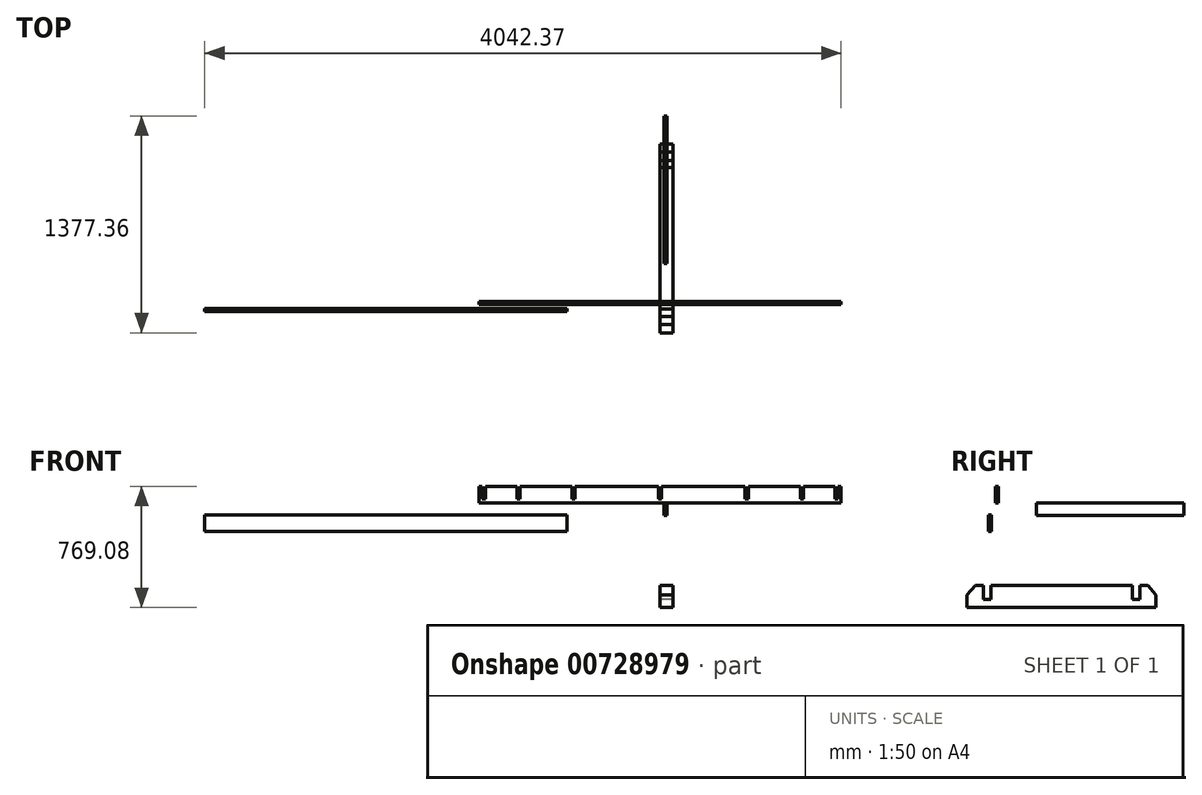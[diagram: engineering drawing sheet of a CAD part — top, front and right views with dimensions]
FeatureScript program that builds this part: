
annotation { "Feature Type Name" : "Feature", "Feature Type Description" : "" }
export const myFeature = defineFeature(function(context is Context, id is Id, definition is map)
    precondition{}
    {
        {
            var Q0;
            Q0=qCreatedBy(makeId("Front.planeOp"),FACE);
            var sketch = newSketch(context, id + "F0", { "sketchPlane" : qUnion([Q0])});
            skLineSegment(sketch, "E0.bottom", {"start": v(0, 0) * mm, "end": v(1150, 0) * mm});
            skLineSegment(sketch, "E0.top", {"start": v(10, 106) * mm, "end": v(540, 106) * mm});
            skLineSegment(sketch, "E0.right", {"start": v(1150, 0) * mm, "end": v(1150, 106) * mm});
            skLineSegment(sketch, "E1.top", {"start": v(0, 26) * mm, "end": v(10, 26) * mm});
            skLineSegment(sketch, "E1.right", {"start": v(10, 106) * mm, "end": v(10, 26) * mm});
            skLineSegment(sketch, "E2.top", {"start": v(540, 26) * mm, "end": v(560, 26) * mm});
            skLineSegment(sketch, "E2.left", {"start": v(540, 106) * mm, "end": v(540, 26) * mm});
            skLineSegment(sketch, "E2.right", {"start": v(560, 106) * mm, "end": v(560, 26) * mm});
            skLineSegment(sketch, "E3.1.0.0", {"start": v(910, 106) * mm, "end": v(910, 26) * mm});
            skLineSegment(sketch, "E3.1.0.1", {"start": v(890, 106) * mm, "end": v(890, 26) * mm});
            skLineSegment(sketch, "E3.1.0.2", {"start": v(890, 26) * mm, "end": v(910, 26) * mm});
            skLineSegment(sketch, "E3.2.0.0", {"start": v(1130, 106) * mm, "end": v(1130, 26) * mm});
            skLineSegment(sketch, "E3.2.0.1", {"start": v(1110, 106) * mm, "end": v(1110, 26) * mm});
            skLineSegment(sketch, "E3.2.0.2", {"start": v(1110, 26) * mm, "end": v(1130, 26) * mm});
            skLineSegment(sketch, "E3.direction1", {"start": v(540, 26) * mm, "end": v(890, 26) * mm, "construction": true});
            skLineSegment(sketch, "E4.trimOffspring", {"start": v(560, 106) * mm, "end": v(890, 106) * mm});
            skLineSegment(sketch, "E5.trimOffspring", {"start": v(910, 106) * mm, "end": v(1110, 106) * mm});
            skLineSegment(sketch, "E6.trimOffspring", {"start": v(1130, 106) * mm, "end": v(1150, 106) * mm});
            skLineSegment(sketch, "E7.MirrorCS", {"start": v(0, 26) * mm, "end": v(-10, 26) * mm});
            skLineSegment(sketch, "E8.MirrorCS", {"start": v(-540, 26) * mm, "end": v(-560, 26) * mm});
            skLineSegment(sketch, "E9.MirrorCS", {"start": v(-890, 26) * mm, "end": v(-910, 26) * mm});
            skLineSegment(sketch, "E10.MirrorCS", {"start": v(-1110, 26) * mm, "end": v(-1130, 26) * mm});
            skLineSegment(sketch, "E11.MirrorCS", {"start": v(-1130, 106) * mm, "end": v(-1150, 106) * mm});
            skLineSegment(sketch, "E12.MirrorCS", {"start": v(-1110, 106) * mm, "end": v(-1110, 26) * mm});
            skLineSegment(sketch, "E13.MirrorCS", {"start": v(-540, 26) * mm, "end": v(-890, 26) * mm, "construction": true});
            skLineSegment(sketch, "E14.MirrorCS", {"start": v(0, 0) * mm, "end": v(-1150, 0) * mm});
            skLineSegment(sketch, "E15.MirrorCS", {"start": v(-10, 106) * mm, "end": v(-540, 106) * mm});
            skLineSegment(sketch, "E16.MirrorCS", {"start": v(-1150, 0) * mm, "end": v(-1150, 106) * mm});
            skLineSegment(sketch, "E17.MirrorCS", {"start": v(-10, 106) * mm, "end": v(-10, 26) * mm});
            skLineSegment(sketch, "E18.MirrorCS", {"start": v(-540, 106) * mm, "end": v(-540, 26) * mm});
            skLineSegment(sketch, "E19.MirrorCS", {"start": v(-560, 106) * mm, "end": v(-560, 26) * mm});
            skLineSegment(sketch, "E20.MirrorCS", {"start": v(-910, 106) * mm, "end": v(-910, 26) * mm});
            skLineSegment(sketch, "E21.MirrorCS", {"start": v(-890, 106) * mm, "end": v(-890, 26) * mm});
            skLineSegment(sketch, "E22.MirrorCS", {"start": v(-1130, 106) * mm, "end": v(-1130, 26) * mm});
            skLineSegment(sketch, "E23.MirrorCS", {"start": v(-560, 106) * mm, "end": v(-890, 106) * mm});
            skLineSegment(sketch, "E24.MirrorCS", {"start": v(-910, 106) * mm, "end": v(-1110, 106) * mm});
            skSolve(sketch);
        }
        {
            var Q0;
            Q0=makeQuery(id+"F0.imprint","IMPRINT",FACE,{"disambiguationData":[TD([[makeQuery(id+"F0.imprint","IMPRINT",EDGE,{"derivedFrom":sQuery(id+"F0.wireOp",EDGE,"E0.bottom")}),1.0]])]});
            extrude(context, id + "F1", {"entities" : qUnion([Q0]), "depth" : 19 * mm, "offsetDistance" : 25 * mm});
        }
        {
            var Q0;
            Q0=makeQuery(id+"F1.opExtrude","CAP_FACE",FACE,{"disambiguationData":[OSD([sQuery(id+"F0.wireOp",EDGE,"E0.bottom"),sQuery(id+"F0.wireOp",EDGE,"E0.top"),sQuery(id+"F0.wireOp",EDGE,"E0.right"),sQuery(id+"F0.wireOp",EDGE,"E1.top"),sQuery(id+"F0.wireOp",EDGE,"E1.right"),sQuery(id+"F0.wireOp",EDGE,"E2.top"),sQuery(id+"F0.wireOp",EDGE,"E2.left"),sQuery(id+"F0.wireOp",EDGE,"E2.right"),sQuery(id+"F0.wireOp",EDGE,"E3.1.0.0"),sQuery(id+"F0.wireOp",EDGE,"E3.1.0.1"),sQuery(id+"F0.wireOp",EDGE,"E3.1.0.2"),sQuery(id+"F0.wireOp",EDGE,"E3.2.0.0"),sQuery(id+"F0.wireOp",EDGE,"E3.2.0.1"),sQuery(id+"F0.wireOp",EDGE,"E3.2.0.2"),sQuery(id+"F0.wireOp",EDGE,"E4.trimOffspring"),sQuery(id+"F0.wireOp",EDGE,"E5.trimOffspring"),sQuery(id+"F0.wireOp",EDGE,"E6.trimOffspring"),sQuery(id+"F0.wireOp",EDGE,"E7.MirrorCS"),sQuery(id+"F0.wireOp",EDGE,"E8.MirrorCS"),sQuery(id+"F0.wireOp",EDGE,"E9.MirrorCS"),sQuery(id+"F0.wireOp",EDGE,"E10.MirrorCS"),sQuery(id+"F0.wireOp",EDGE,"E11.MirrorCS"),sQuery(id+"F0.wireOp",EDGE,"E12.MirrorCS"),sQuery(id+"F0.wireOp",EDGE,"E14.MirrorCS"),sQuery(id+"F0.wireOp",EDGE,"E15.MirrorCS"),sQuery(id+"F0.wireOp",EDGE,"E16.MirrorCS"),sQuery(id+"F0.wireOp",EDGE,"E17.MirrorCS"),sQuery(id+"F0.wireOp",EDGE,"E18.MirrorCS"),sQuery(id+"F0.wireOp",EDGE,"E19.MirrorCS"),sQuery(id+"F0.wireOp",EDGE,"E20.MirrorCS"),sQuery(id+"F0.wireOp",EDGE,"E21.MirrorCS"),sQuery(id+"F0.wireOp",EDGE,"E22.MirrorCS"),sQuery(id+"F0.wireOp",EDGE,"E23.MirrorCS"),sQuery(id+"F0.wireOp",EDGE,"E24.MirrorCS")])],"isStart":false});
            cPlane(context, id + "F2", {"entities" : qUnion([Q0]), "cplaneType" : CPlaneType.OFFSET, "offset" : 25 * mm, "width" : 150 * mm, "height" : 150 * mm});
        }
        {
            var Q0;
            Q0=qCreatedBy(id+"F2.planeOp",FACE);
            var sketch = newSketch(context, id + "F3", { "sketchPlane" : qUnion([Q0])});
            skLineSegment(sketch, "E25.bottom", {"start": v(-2892.37, -75.37) * mm, "end": v(-592.37, -75.37) * mm});
            skLineSegment(sketch, "E25.top", {"start": v(-2892.37, -181.37) * mm, "end": v(-592.37, -181.37) * mm});
            skLineSegment(sketch, "E25.left", {"start": v(-2892.37, -75.37) * mm, "end": v(-2892.37, -181.37) * mm});
            skLineSegment(sketch, "E25.right", {"start": v(-592.37, -75.37) * mm, "end": v(-592.37, -181.37) * mm});
            skSolve(sketch);
        }
        {
            var Q0;
            Q0=makeQuery(id+"F3.imprint","IMPRINT",FACE,{"disambiguationData":[TD([[makeQuery(id+"F3.imprint","IMPRINT",EDGE,{"derivedFrom":sQuery(id+"F3.wireOp",EDGE,"E25.bottom")}),-1.0]])]});
            extrude(context, id + "F4", {"entities" : qUnion([Q0]), "depth" : 19 * mm, "offsetDistance" : 25 * mm});
        }
        {
            var Q0;
            Q0=qCreatedBy(makeId("Right.planeOp"),FACE);
            var sketch = newSketch(context, id + "F5", { "sketchPlane" : qUnion([Q0])});
            skLineSegment(sketch, "E26.bottom", {"start": v(-146.67, -523.08) * mm, "end": v(-94.67, -523.08) * mm});
            skLineSegment(sketch, "E26.top", {"start": v(-198.67, -663.08) * mm, "end": v(1001.33, -663.08) * mm});
            skLineSegment(sketch, "E26.left", {"start": v(-198.67, -583.08) * mm, "end": v(-198.67, -663.08) * mm});
            skLineSegment(sketch, "E26.right", {"start": v(1001.33, -583.08) * mm, "end": v(1001.33, -663.08) * mm});
            skLineSegment(sketch, "E27.top", {"start": v(850.33, -613.08) * mm, "end": v(897.33, -613.08) * mm});
            skLineSegment(sketch, "E27.left", {"start": v(850.33, -523.08) * mm, "end": v(850.33, -613.08) * mm});
            skLineSegment(sketch, "E27.right", {"start": v(897.33, -523.08) * mm, "end": v(897.33, -613.08) * mm});
            skPoint(sketch, "E28", {"position": v(401.33, -523.08) * mm});
            skLineSegment(sketch, "E29.trimOffspring", {"start": v(897.33, -523.08) * mm, "end": v(949.33, -523.08) * mm});
            skLineSegment(sketch, "E30", {"start": v(949.33, -523.08) * mm, "end": v(1001.33, -583.08) * mm});
            skPoint(sketch, "E31.orphan", {"position": v(1001.33, -523.08) * mm});
            skLineSegment(sketch, "E32", {"start": v(401.33, -523.08) * mm, "end": v(401.33, -719.43) * mm, "construction": true});
            skLineSegment(sketch, "E33.MirrorCS", {"start": v(-94.67, -523.08) * mm, "end": v(-94.67, -613.08) * mm});
            skLineSegment(sketch, "E34.MirrorCS", {"start": v(-146.67, -523.08) * mm, "end": v(-198.67, -583.08) * mm});
            skLineSegment(sketch, "E35.MirrorCS", {"start": v(-47.67, -523.08) * mm, "end": v(-47.67, -613.08) * mm});
            skLineSegment(sketch, "E36.MirrorCS", {"start": v(-94.67, -523.08) * mm, "end": v(-146.67, -523.08) * mm});
            skLineSegment(sketch, "E37.MirrorCS", {"start": v(-47.67, -613.08) * mm, "end": v(-94.67, -613.08) * mm});
            skPoint(sketch, "E38.MirrorP", {"position": v(-198.67, -523.08) * mm});
            skLineSegment(sketch, "E39.trimOffspring", {"start": v(-47.67, -523.08) * mm, "end": v(850.33, -523.08) * mm});
            skSolve(sketch);
        }
        {
            var Q0;
            Q0=makeQuery(id+"F5.imprint","IMPRINT",FACE,{"disambiguationData":[TD([[makeQuery(id+"F5.imprint","IMPRINT",EDGE,{"derivedFrom":sQuery(id+"F5.wireOp",EDGE,"E26.top")}),1.0]])]});
            extrude(context, id + "F6", {"entities" : qUnion([Q0]), "depth" : 82 * mm, "offsetDistance" : 25 * mm});
        }
        {
            var Q0;
            Q0=qCreatedBy(makeId("Right.planeOp"),FACE);
            cPlane(context, id + "F7", {"entities" : qUnion([Q0]), "cplaneType" : CPlaneType.OFFSET, "offset" : 25 * mm, "width" : 150 * mm, "height" : 150 * mm});
        }
        {
            var Q0;
            Q0=qCreatedBy(id+"F7.planeOp",FACE);
            var sketch = newSketch(context, id + "F8", { "sketchPlane" : qUnion([Q0])});
            skLineSegment(sketch, "E40.bottom", {"start": v(242.7, 0) * mm, "end": v(1178.7, 0) * mm});
            skLineSegment(sketch, "E40.top", {"start": v(242.7, -80) * mm, "end": v(1178.7, -80) * mm});
            skLineSegment(sketch, "E40.left", {"start": v(242.7, 0) * mm, "end": v(242.7, -80) * mm});
            skLineSegment(sketch, "E40.right", {"start": v(1178.7, 0) * mm, "end": v(1178.7, -80) * mm});
            skSolve(sketch);
        }
        {
            var Q0;
            Q0=makeQuery(id+"F8.imprint","IMPRINT",FACE,{"disambiguationData":[TD([[makeQuery(id+"F8.imprint","IMPRINT",EDGE,{"derivedFrom":sQuery(id+"F8.wireOp",EDGE,"E40.bottom")}),-1.0]])]});
            extrude(context, id + "F9", {"entities" : qUnion([Q0]), "depth" : 19 * mm, "offsetDistance" : 25 * mm});
        }
    });
